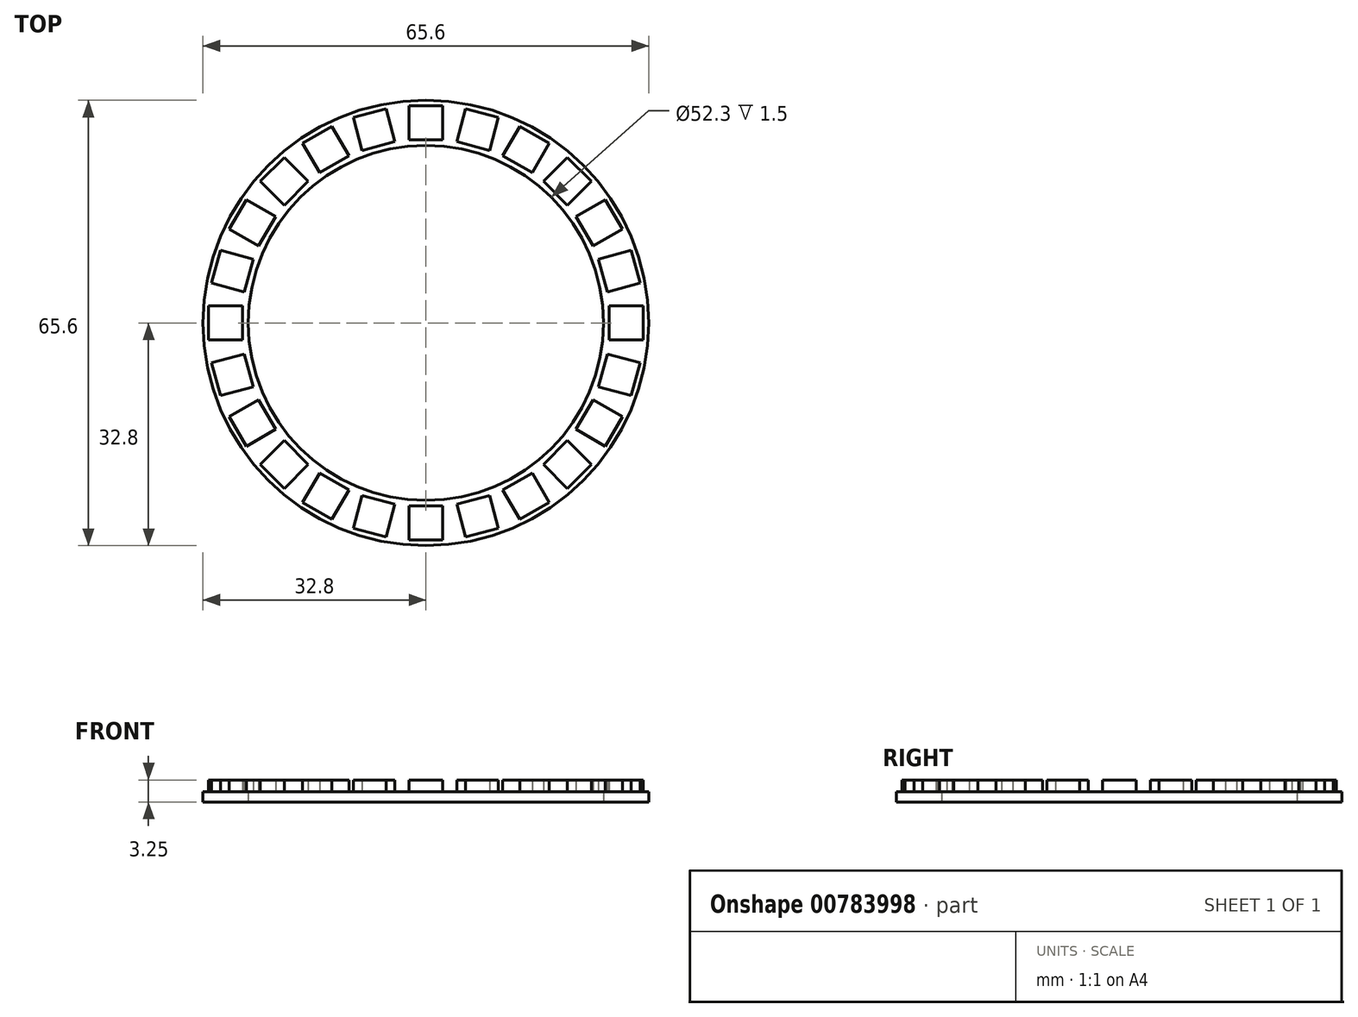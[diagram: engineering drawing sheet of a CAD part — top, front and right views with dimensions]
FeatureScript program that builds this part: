
annotation { "Feature Type Name" : "Feature", "Feature Type Description" : "" }
export const myFeature = defineFeature(function(context is Context, id is Id, definition is map)
    precondition{}
    {
        {
            var Q0;
            Q0=qCreatedBy(makeId("Top.planeOp"),FACE);
            var sketch = newSketch(context, id + "F0", { "sketchPlane" : qUnion([Q0])});
            skCircle(sketch, "E0", {"center": v(0, 0) * mm, "radius": 32.8 * mm});
            skCircle(sketch, "E1", {"center": v(0, 0) * mm, "radius": 26.15 * mm});
            skSolve(sketch);
        }
        {
            var Q0;
            Q0=qCreatedBy(makeId("Top.planeOp"),FACE);
            var sketch = newSketch(context, id + "F1", { "sketchPlane" : qUnion([Q0])});
            skLineSegment(sketch, "E2", {"start": v(0, 26.15) * mm, "end": v(0, 32.8) * mm});
            skLineSegment(sketch, "E3.bottom", {"start": v(2.5, 31.97) * mm, "end": v(-2.5, 31.97) * mm});
            skLineSegment(sketch, "E3.top", {"start": v(2.5, 26.97) * mm, "end": v(-2.5, 26.97) * mm});
            skLineSegment(sketch, "E3.left", {"start": v(2.5, 31.97) * mm, "end": v(2.5, 26.97) * mm});
            skLineSegment(sketch, "E3.right", {"start": v(-2.5, 31.97) * mm, "end": v(-2.5, 26.97) * mm});
            skPoint(sketch, "E3.middle", {"position": v(0, 29.47) * mm});
            skSolve(sketch);
        }
        {
            var Q0;
            Q0=makeQuery(id+"F0.imprint","IMPRINT",FACE,{"disambiguationData":[TD([[makeQuery(id+"F0.imprint","IMPRINT",EDGE,{"derivedFrom":sQuery(id+"F0.wireOp",EDGE,"E0")}),1.0]])]});
            extrude(context, id + "F2", {"entities" : qUnion([Q0]), "depth" : 1.5 * mm, "offsetDistance" : 25 * mm});
        }
        {
            var Q0;
            {var subQ5=sQuery(id+"F1.wireOp",EDGE,"E3.right");Q0=makeQuery(id+"F1.imprint","IMPRINT",FACE,{"disambiguationData":[TD([[makeQuery(id+"F1.imprint","IMPRINT",EDGE,{"derivedFrom":subQ5}),1.0]])]});}
            var Q1;
            {var subQ5=sQuery(id+"F1.wireOp",EDGE,"E3.left");Q1=makeQuery(id+"F1.imprint","IMPRINT",FACE,{"disambiguationData":[TD([[makeQuery(id+"F1.imprint","IMPRINT",EDGE,{"derivedFrom":subQ5}),-1.0]])]});}
            extrude(context, id + "F3", {"entities" : qUnion([Q0, Q1]), "depth" : 3.25 * mm, "offsetDistance" : 25 * mm});
        }
        {
            var Q0;
            Q0=makeQuery(id+"F3.opExtrude","SWEPT_BODY",BODY,{"disambiguationData":[OSD([sQuery(id+"F1.wireOp",EDGE,"E3.bottom"),sQuery(id+"F1.wireOp",EDGE,"E3.top"),sQuery(id+"F1.wireOp",EDGE,"E3.left"),sQuery(id+"F1.wireOp",EDGE,"E3.right")])]});
            var Q1;
            Q1=sQuery(id+"F0.wireOp",EDGE,"E1");
            circularPattern(context, id + "F4", {"operationType" : NewBodyOperationType.ADD, "entities" : qUnion([Q0]), "axis" : qUnion([Q1]), "angle" : 360 * degree, "instanceCount" : 24, "equalSpace" : true});
        }
    });
